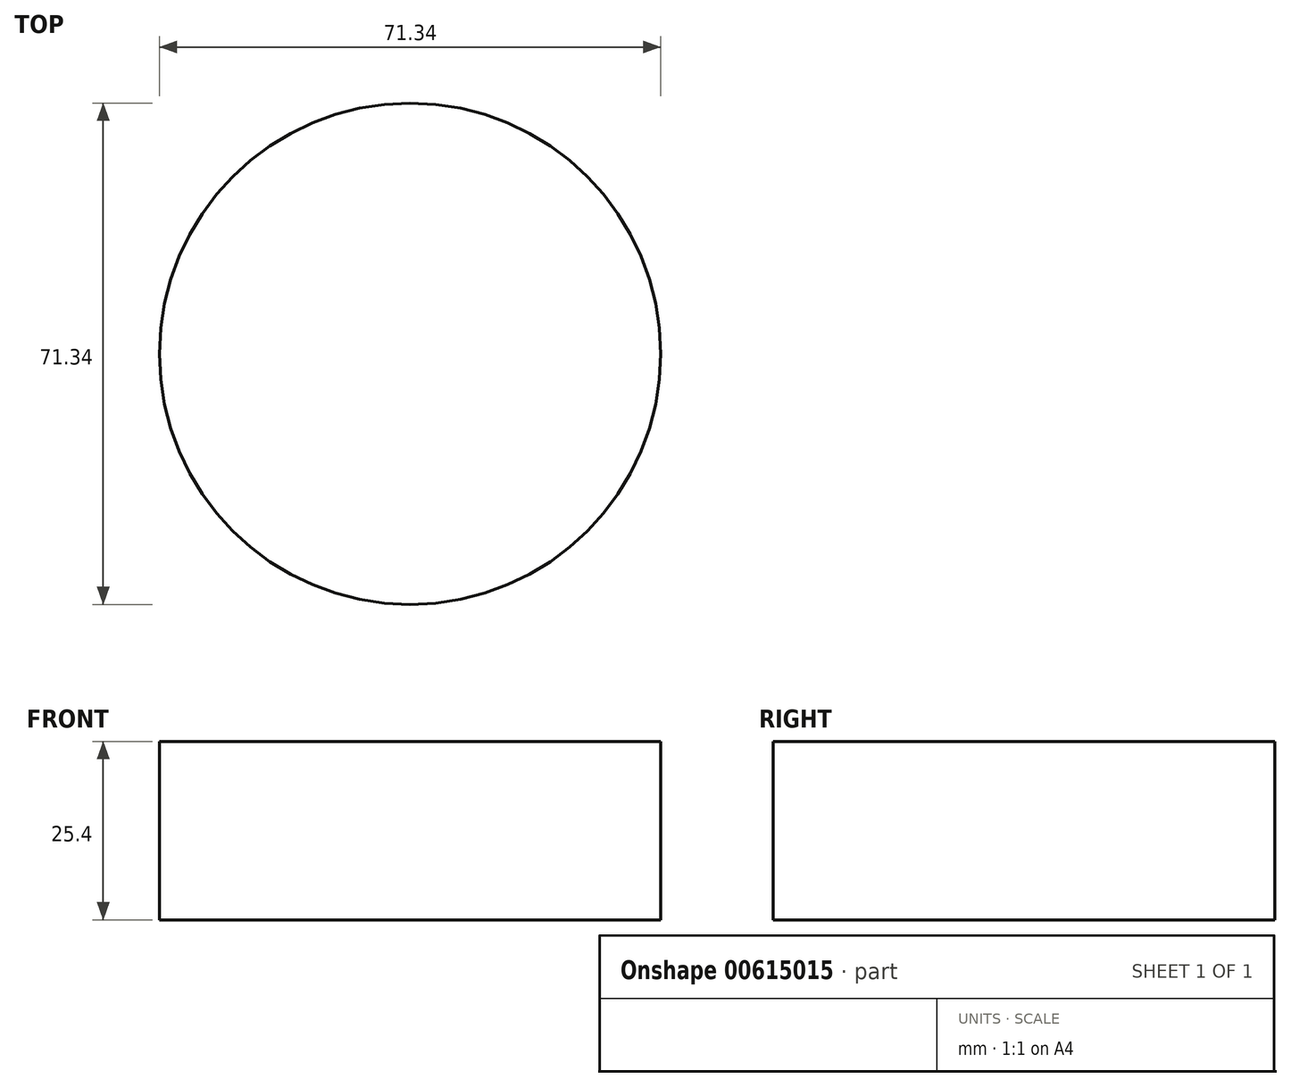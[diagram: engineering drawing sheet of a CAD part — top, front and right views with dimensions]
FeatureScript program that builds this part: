
annotation { "Feature Type Name" : "Feature", "Feature Type Description" : "" }
export const myFeature = defineFeature(function(context is Context, id is Id, definition is map)
    precondition{}
    {
        {
            var Q0;
            Q0=qCreatedBy(makeId("Top.planeOp"),FACE);
            var sketch = newSketch(context, id + "F0", { "sketchPlane" : qUnion([Q0])});
            skCircle(sketch, "E0", {"center": v(0, 0) * mm, "radius": 35.67 * mm});
            skSolve(sketch);
        }
        {
            var Q0;
            Q0=makeQuery(id+"F0.imprint","IMPRINT",FACE,{"disambiguationData":[TD([[makeQuery(id+"F0.imprint","IMPRINT",EDGE,{"derivedFrom":sQuery(id+"F0.wireOp",EDGE,"E0")}),1.0]])]});
            extrude(context, id + "F1", {"entities" : qUnion([Q0]), "depth" : 25.4 * mm, "offsetDistance" : 25.4 * mm});
        }
    });
